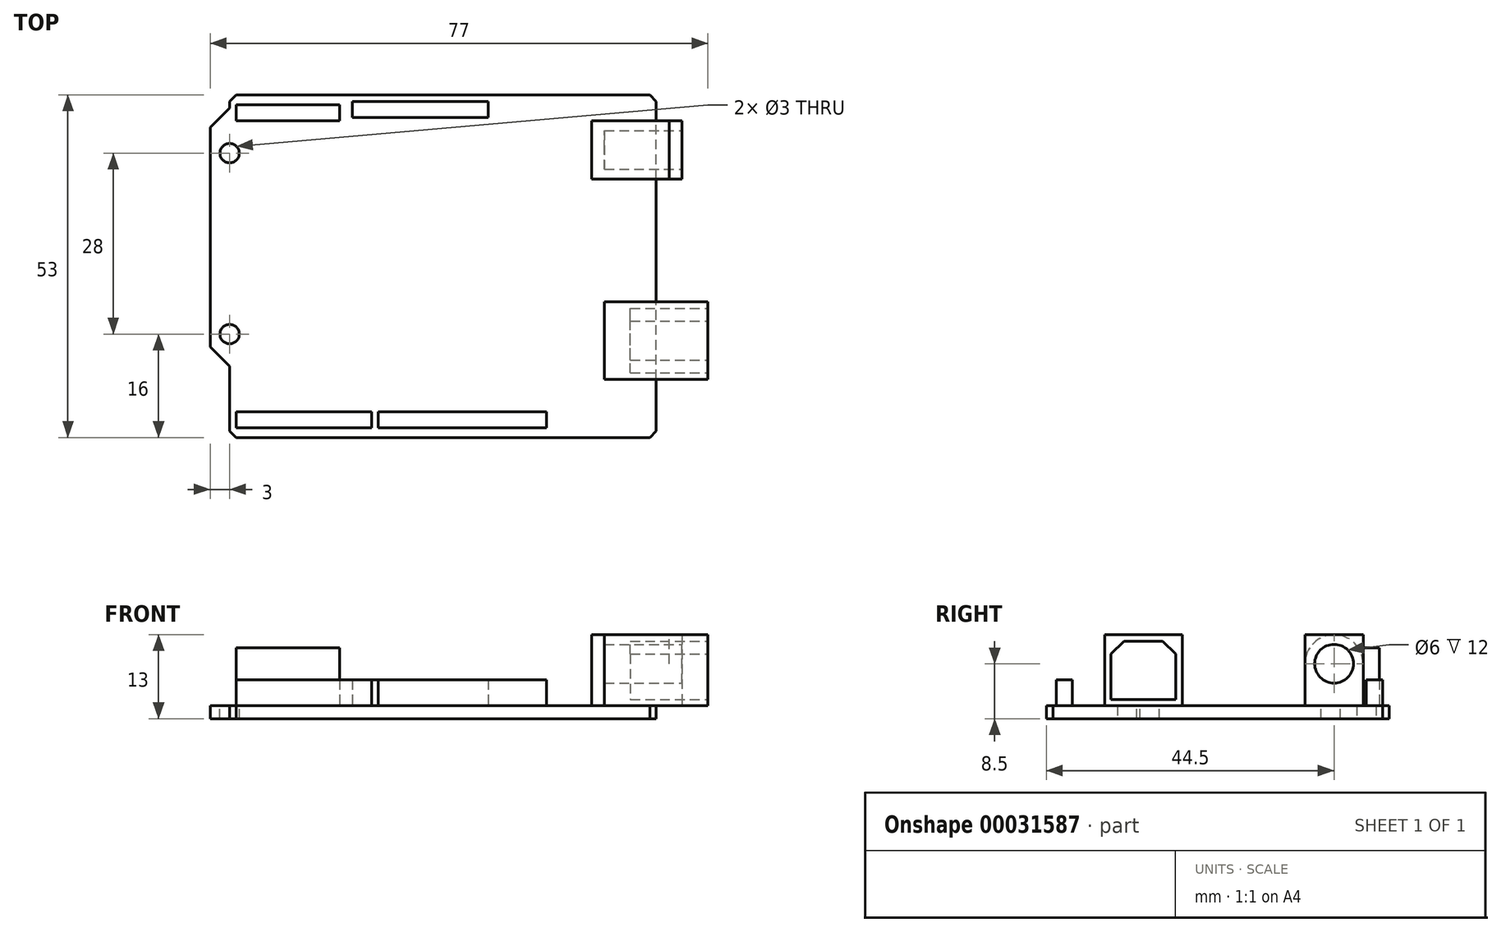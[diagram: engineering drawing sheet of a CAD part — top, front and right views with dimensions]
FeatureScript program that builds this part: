
annotation { "Feature Type Name" : "Feature", "Feature Type Description" : "" }
export const myFeature = defineFeature(function(context is Context, id is Id, definition is map)
    precondition{}
    {
        {
            var Q0;
            Q0=qCreatedBy(makeId("Top.planeOp"),FACE);
            var sketch = newSketch(context, id + "F0", { "sketchPlane" : qUnion([Q0])});
            skLineSegment(sketch, "E0.bottom", {"start": v(3, 0) * mm, "end": v(69, 0) * mm});
            skLineSegment(sketch, "E0.top", {"start": v(3, 53) * mm, "end": v(69, 53) * mm});
            skLineSegment(sketch, "E0.left", {"start": v(0, 11) * mm, "end": v(0, 51) * mm});
            skLineSegment(sketch, "E0.right", {"start": v(69, 0) * mm, "end": v(69, 53) * mm});
            skLineSegment(sketch, "E1", {"start": v(3, 53) * mm, "end": v(3, 51) * mm});
            skLineSegment(sketch, "E2", {"start": v(3, 51) * mm, "end": v(0, 51) * mm});
            skLineSegment(sketch, "E3.top", {"start": v(0, 11) * mm, "end": v(3, 11) * mm});
            skLineSegment(sketch, "E3.right", {"start": v(3, 0) * mm, "end": v(3, 11) * mm});
            skSolve(sketch);
        }
        {
            var Q0;
            Q0 = qSketchRegion(id + "F0", true);
            extrude(context, id + "F1", {"entities" : qUnion([Q0]), "depth" : 2 * mm});
        }
        {
            var Q0;
            Q0=makeQuery(id+"F1.opExtrude","CAP_FACE",FACE,{"disambiguationData":[OSD([sQuery(id+"F0.wireOp",EDGE,"E0.bottom"),sQuery(id+"F0.wireOp",EDGE,"E0.top"),sQuery(id+"F0.wireOp",EDGE,"E0.left"),sQuery(id+"F0.wireOp",EDGE,"E0.right"),sQuery(id+"F0.wireOp",EDGE,"E1"),sQuery(id+"F0.wireOp",EDGE,"E2"),sQuery(id+"F0.wireOp",EDGE,"E3.top"),sQuery(id+"F0.wireOp",EDGE,"E3.right")])],"isStart":false});
            var sketch = newSketch(context, id + "F2", { "sketchPlane" : qUnion([Q0])});
            skLineSegment(sketch, "E4.bottom", {"start": v(61, 21) * mm, "end": v(77, 21) * mm});
            skLineSegment(sketch, "E4.top", {"start": v(61, 9) * mm, "end": v(77, 9) * mm});
            skLineSegment(sketch, "E4.left", {"start": v(61, 21) * mm, "end": v(61, 9) * mm});
            skLineSegment(sketch, "E4.right", {"start": v(77, 21) * mm, "end": v(77, 9) * mm});
            skSolve(sketch);
        }
        {
            var Q0;
            Q0 = qSketchRegion(id + "F2", true);
            extrude(context, id + "F3", {"entities" : qUnion([Q0]), "operationType" : NewBodyOperationType.ADD, "depth" : 11 * mm});
        }
        {
            var Q0;
            Q0=makeQuery(id+"F1.opExtrude","CAP_FACE",FACE,{"disambiguationData":[OSD([sQuery(id+"F0.wireOp",EDGE,"E0.bottom"),sQuery(id+"F0.wireOp",EDGE,"E0.top"),sQuery(id+"F0.wireOp",EDGE,"E0.left"),sQuery(id+"F0.wireOp",EDGE,"E0.right"),sQuery(id+"F0.wireOp",EDGE,"E1"),sQuery(id+"F0.wireOp",EDGE,"E2"),sQuery(id+"F0.wireOp",EDGE,"E3.top"),sQuery(id+"F0.wireOp",EDGE,"E3.right")])],"isStart":false});
            var sketch = newSketch(context, id + "F4", { "sketchPlane" : qUnion([Q0])});
            skLineSegment(sketch, "E5.bottom", {"start": v(59, 49) * mm, "end": v(73, 49) * mm});
            skLineSegment(sketch, "E5.top", {"start": v(59, 40) * mm, "end": v(73, 40) * mm});
            skLineSegment(sketch, "E5.left", {"start": v(59, 49) * mm, "end": v(59, 40) * mm});
            skLineSegment(sketch, "E5.right", {"start": v(73, 49) * mm, "end": v(73, 40) * mm});
            skSolve(sketch);
        }
        {
            var Q0;
            Q0 = qSketchRegion(id + "F4", true);
            extrude(context, id + "F5", {"entities" : qUnion([Q0]), "operationType" : NewBodyOperationType.ADD, "depth" : 11 * mm});
        }
        {
            var Q0;
            Q0=makeQuery(id+"F1.opExtrude","CAP_FACE",FACE,{"disambiguationData":[OSD([sQuery(id+"F0.wireOp",EDGE,"E0.bottom"),sQuery(id+"F0.wireOp",EDGE,"E0.top"),sQuery(id+"F0.wireOp",EDGE,"E0.left"),sQuery(id+"F0.wireOp",EDGE,"E0.right"),sQuery(id+"F0.wireOp",EDGE,"E1"),sQuery(id+"F0.wireOp",EDGE,"E2"),sQuery(id+"F0.wireOp",EDGE,"E3.top"),sQuery(id+"F0.wireOp",EDGE,"E3.right")])],"isStart":false});
            var sketch = newSketch(context, id + "F6", { "sketchPlane" : qUnion([Q0])});
            skLineSegment(sketch, "E6.bottom", {"start": v(4, 51.5) * mm, "end": v(20, 51.5) * mm});
            skLineSegment(sketch, "E6.top", {"start": v(4, 49) * mm, "end": v(20, 49) * mm});
            skLineSegment(sketch, "E6.left", {"start": v(4, 51.5) * mm, "end": v(4, 49) * mm});
            skLineSegment(sketch, "E6.right", {"start": v(20, 51.5) * mm, "end": v(20, 49) * mm});
            skSolve(sketch);
        }
        {
            var Q0;
            Q0 = qSketchRegion(id + "F6", true);
            extrude(context, id + "F7", {"entities" : qUnion([Q0]), "operationType" : NewBodyOperationType.ADD, "depth" : 9 * mm});
        }
        {
            var Q0;
            Q0=makeQuery(id+"F1.opExtrude","CAP_FACE",FACE,{"disambiguationData":[OSD([sQuery(id+"F0.wireOp",EDGE,"E0.bottom"),sQuery(id+"F0.wireOp",EDGE,"E0.top"),sQuery(id+"F0.wireOp",EDGE,"E0.left"),sQuery(id+"F0.wireOp",EDGE,"E0.right"),sQuery(id+"F0.wireOp",EDGE,"E1"),sQuery(id+"F0.wireOp",EDGE,"E2"),sQuery(id+"F0.wireOp",EDGE,"E3.top"),sQuery(id+"F0.wireOp",EDGE,"E3.right")])],"isStart":false});
            var sketch = newSketch(context, id + "F8", { "sketchPlane" : qUnion([Q0])});
            skLineSegment(sketch, "E7.bottom", {"start": v(22, 52) * mm, "end": v(43, 52) * mm});
            skLineSegment(sketch, "E7.top", {"start": v(22, 49.5) * mm, "end": v(43, 49.5) * mm});
            skLineSegment(sketch, "E7.left", {"start": v(22, 52) * mm, "end": v(22, 49.5) * mm});
            skLineSegment(sketch, "E7.right", {"start": v(43, 52) * mm, "end": v(43, 49.5) * mm});
            skSolve(sketch);
        }
        {
            var Q0;
            Q0 = qSketchRegion(id + "F8", true);
            extrude(context, id + "F9", {"entities" : qUnion([Q0]), "operationType" : NewBodyOperationType.ADD, "depth" : 4 * mm});
        }
        {
            var Q0;
            Q0=makeQuery(id+"F1.opExtrude","CAP_FACE",FACE,{"disambiguationData":[OSD([sQuery(id+"F0.wireOp",EDGE,"E0.bottom"),sQuery(id+"F0.wireOp",EDGE,"E0.top"),sQuery(id+"F0.wireOp",EDGE,"E0.left"),sQuery(id+"F0.wireOp",EDGE,"E0.right"),sQuery(id+"F0.wireOp",EDGE,"E1"),sQuery(id+"F0.wireOp",EDGE,"E2"),sQuery(id+"F0.wireOp",EDGE,"E3.top"),sQuery(id+"F0.wireOp",EDGE,"E3.right")])],"isStart":false});
            var sketch = newSketch(context, id + "F10", { "sketchPlane" : qUnion([Q0])});
            skLineSegment(sketch, "E8.bottom", {"start": v(4, 4) * mm, "end": v(25, 4) * mm});
            skLineSegment(sketch, "E8.top", {"start": v(4, 1.5) * mm, "end": v(25, 1.5) * mm});
            skLineSegment(sketch, "E8.left", {"start": v(4, 4) * mm, "end": v(4, 1.5) * mm});
            skLineSegment(sketch, "E8.right", {"start": v(25, 4) * mm, "end": v(25, 1.5) * mm});
            skLineSegment(sketch, "E9.bottom", {"start": v(26, 4) * mm, "end": v(52, 4) * mm});
            skLineSegment(sketch, "E9.top", {"start": v(26, 1.5) * mm, "end": v(52, 1.5) * mm});
            skLineSegment(sketch, "E9.left", {"start": v(26, 4) * mm, "end": v(26, 1.5) * mm});
            skLineSegment(sketch, "E9.right", {"start": v(52, 4) * mm, "end": v(52, 1.5) * mm});
            skSolve(sketch);
        }
        {
            var Q0;
            Q0 = qSketchRegion(id + "F10", true);
            extrude(context, id + "F11", {"entities" : qUnion([Q0]), "operationType" : NewBodyOperationType.ADD, "depth" : 4 * mm});
        }
        {
            var Q0;
            Q0=makeQuery(id+"F5.opExtrude","SWEPT_FACE",FACE,{"disambiguationData":[OSD([sQuery(id+"F4.wireOp",EDGE,"E5.left")])]});
            var sketch = newSketch(context, id + "F12", { "sketchPlane" : qUnion([Q0])});
            skArc(sketch, "E10", {"start": v(-40, 8.5) * mm, "mid": v(-44.5, 13) * mm, "end": v(-49, 8.5) * mm});
            skLineSegment(sketch, "E11", {"start": v(-49, 8.5) * mm, "end": v(-51.25, 13.88) * mm});
            skLineSegment(sketch, "E12", {"start": v(-51.25, 13.88) * mm, "end": v(-42.27, 14.8) * mm});
            skLineSegment(sketch, "E13", {"start": v(-42.27, 14.8) * mm, "end": v(-38.19, 14.06) * mm});
            skLineSegment(sketch, "E14", {"start": v(-38.19, 14.06) * mm, "end": v(-38.63, 9.58) * mm});
            skLineSegment(sketch, "E15", {"start": v(-38.63, 9.58) * mm, "end": v(-40, 8.5) * mm});
            skSolve(sketch);
        }
        {
            var Q0;
            Q0 = qSketchRegion(id + "F12", true);
            var Q1;
            {var subQ9=sQuery(id+"F12.wireOp",EDGE,"E11");Q1=makeQuery(id+"F12.imprint","IMPRINT",FACE,{"disambiguationData":[TD([[makeQuery(id+"F12.imprint","IMPRINT",EDGE,{"derivedFrom":subQ9}),-1.0]])]});}
            extrude(context, id + "F13", {"entities" : qUnion([Q0, Q1]), "operationType" : NewBodyOperationType.REMOVE, "oppositeDirection" : true, "depth" : (14 - 2) * mm});
        }
        {
            var Q0;
            Q0=makeQuery(id+"F5.opExtrude","SWEPT_FACE",FACE,{"disambiguationData":[OSD([sQuery(id+"F4.wireOp",EDGE,"E5.right")])]});
            var sketch = newSketch(context, id + "F14", { "sketchPlane" : qUnion([Q0])});
            skPoint(sketch, "E16.centerSnap0", {"position": v(40, 7.5) * mm});
            skPoint(sketch, "E16.centerSnap1", {"position": v(44.5, 13) * mm});
            skCircle(sketch, "E17", {"center": v(44.5, 8.5) * mm, "radius": 3 * mm});
            skSolve(sketch);
        }
        {
            var Q0;
            Q0 = qSketchRegion(id + "F14", true);
            extrude(context, id + "F15", {"entities" : qUnion([Q0]), "operationType" : NewBodyOperationType.REMOVE, "oppositeDirection" : true, "depth" : 12 * mm});
        }
        {
            var Q0;
            Q0=makeQuery(id+"F3.opExtrude","SWEPT_FACE",FACE,{"disambiguationData":[OSD([sQuery(id+"F2.wireOp",EDGE,"E4.right")])]});
            var sketch = newSketch(context, id + "F16", { "sketchPlane" : qUnion([Q0])});
            skLineSegment(sketch, "E18.bottom", {"start": v(12, 12) * mm, "end": v(18, 12) * mm});
            skLineSegment(sketch, "E18.top", {"start": v(10, 3) * mm, "end": v(20, 3) * mm});
            skLineSegment(sketch, "E18.left", {"start": v(10, 10) * mm, "end": v(10, 3) * mm});
            skLineSegment(sketch, "E18.right", {"start": v(20, 10) * mm, "end": v(20, 3) * mm});
            skLineSegment(sketch, "E19", {"start": v(10, 10) * mm, "end": v(12, 12) * mm});
            skLineSegment(sketch, "E20", {"start": v(18, 12) * mm, "end": v(20, 10) * mm});
            skPoint(sketch, "E21.orphan", {"position": v(20, 12) * mm});
            skSolve(sketch);
        }
        {
            var Q0;
            Q0 = qSketchRegion(id + "F16", true);
            extrude(context, id + "F17", {"entities" : qUnion([Q0]), "operationType" : NewBodyOperationType.REMOVE, "oppositeDirection" : true, "depth" : 12 * mm});
        }
        {
            var Q0;
            Q0=makeQuery(id+"F1.opExtrude","SWEPT_EDGE",EDGE,{"disambiguationData":[OSD([sQuery(id+"F0.wireOp",EDGE,"E0.left"),sQuery(id+"F0.wireOp",EDGE,"E2")])]});
            var Q1;
            Q1=makeQuery(id+"F1.opExtrude","SWEPT_EDGE",EDGE,{"disambiguationData":[OSD([sQuery(id+"F0.wireOp",EDGE,"E0.left"),sQuery(id+"F0.wireOp",EDGE,"E3.top")])]});
            chamfer(context, id + "F18", {"entities" : qUnion([Q0, Q1]), "chamferType" : ChamferType.TWO_OFFSETS, "width1" : 3 * mm, "oppositeDirection" : false, "width2" : 3 * mm, "tangentPropagation" : true});
        }
        {
            var Q0;
            Q0=makeQuery(id+"F1.opExtrude","SWEPT_EDGE",EDGE,{"disambiguationData":[OSD([sQuery(id+"F0.wireOp",EDGE,"E0.bottom"),sQuery(id+"F0.wireOp",EDGE,"E3.right")])]});
            var Q1;
            Q1=makeQuery(id+"F1.opExtrude","SWEPT_EDGE",EDGE,{"disambiguationData":[OSD([sQuery(id+"F0.wireOp",EDGE,"E0.bottom"),sQuery(id+"F0.wireOp",EDGE,"E0.right")])]});
            var Q2;
            Q2=makeQuery(id+"F1.opExtrude","SWEPT_EDGE",EDGE,{"disambiguationData":[OSD([sQuery(id+"F0.wireOp",EDGE,"E0.top"),sQuery(id+"F0.wireOp",EDGE,"E0.right")])]});
            var Q3;
            Q3=makeQuery(id+"F1.opExtrude","SWEPT_EDGE",EDGE,{"disambiguationData":[OSD([sQuery(id+"F0.wireOp",EDGE,"E0.top"),sQuery(id+"F0.wireOp",EDGE,"E1")])]});
            chamfer(context, id + "F19", {"entities" : qUnion([Q0, Q1, Q2, Q3]), "chamferType" : ChamferType.TWO_OFFSETS, "width1" : 1 * mm, "oppositeDirection" : false, "width2" : 1 * mm, "tangentPropagation" : true});
        }
        {
            var Q0;
            Q0=makeQuery(id+"F1.opExtrude","CAP_FACE",FACE,{"disambiguationData":[OSD([sQuery(id+"F0.wireOp",EDGE,"E0.bottom"),sQuery(id+"F0.wireOp",EDGE,"E0.top"),sQuery(id+"F0.wireOp",EDGE,"E0.left"),sQuery(id+"F0.wireOp",EDGE,"E0.right"),sQuery(id+"F0.wireOp",EDGE,"E1"),sQuery(id+"F0.wireOp",EDGE,"E2"),sQuery(id+"F0.wireOp",EDGE,"E3.top"),sQuery(id+"F0.wireOp",EDGE,"E3.right")])],"isStart":false});
            var sketch = newSketch(context, id + "F20", { "sketchPlane" : qUnion([Q0])});
            skCircle(sketch, "E22", {"center": v(3, 16) * mm, "radius": 1.5 * mm});
            skCircle(sketch, "E23", {"center": v(3, 44) * mm, "radius": 1.5 * mm});
            skSolve(sketch);
        }
        {
            var Q0;
            Q0=makeQuery(id+"F20.imprint","IMPRINT",FACE,{"disambiguationData":[TD([[makeQuery(id+"F20.imprint","IMPRINT",EDGE,{"derivedFrom":sQuery(id+"F20.wireOp",EDGE,"E22")}),1.0]])]});
            var Q1;
            Q1=makeQuery(id+"F20.imprint","IMPRINT",FACE,{"disambiguationData":[TD([[makeQuery(id+"F20.imprint","IMPRINT",EDGE,{"derivedFrom":sQuery(id+"F20.wireOp",EDGE,"E23")}),1.0]])]});
            var Q2;
            Q2=sQuery(id+"F20.wireOp",EDGE,"E23");
            extrude(context, id + "F21", {"entities" : qUnion([Q0, Q1]), "operationType" : NewBodyOperationType.REMOVE, "surfaceEntities" : qUnion([Q2]), "oppositeDirection" : true, "depth" : 2 * mm});
        }
    });
